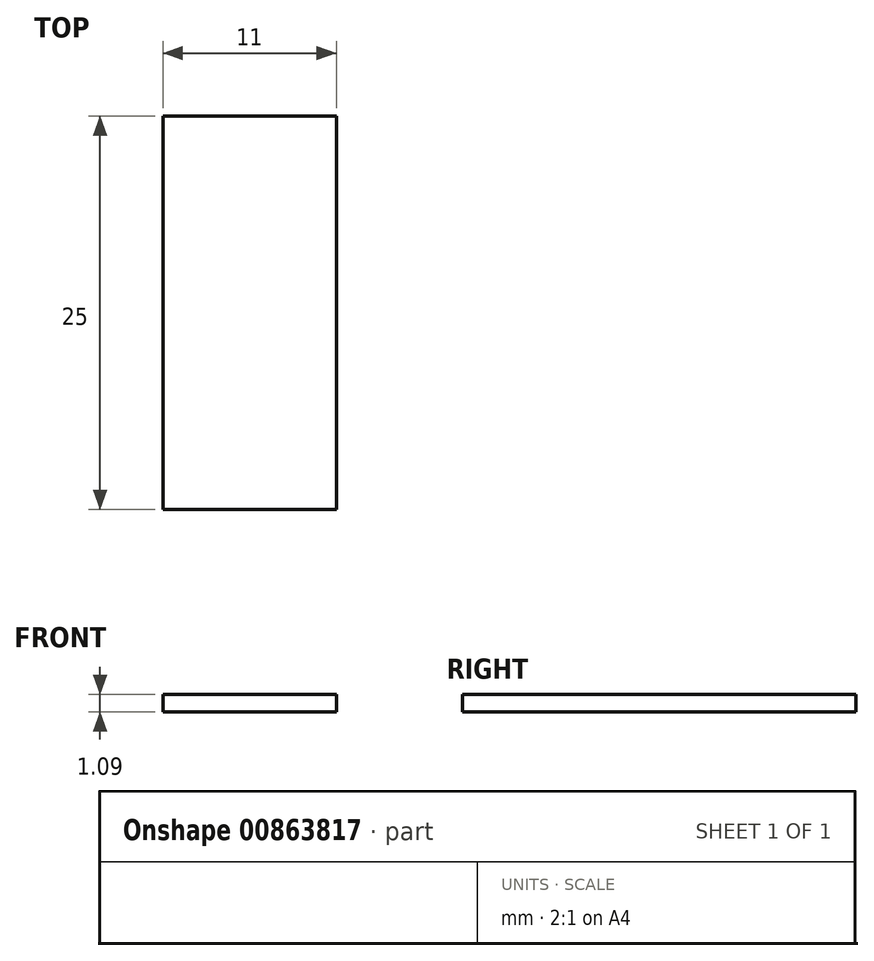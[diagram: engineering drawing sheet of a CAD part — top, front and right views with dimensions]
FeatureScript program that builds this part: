
annotation { "Feature Type Name" : "Feature", "Feature Type Description" : "" }
export const myFeature = defineFeature(function(context is Context, id is Id, definition is map)
    precondition{}
    {
        {
            var Q0;
            Q0=qCreatedBy(makeId("Top.planeOp"),FACE);
            var sketch = newSketch(context, id + "F0", { "sketchPlane" : qUnion([Q0])});
            skLineSegment(sketch, "E0.bottom", {"start": v(0, 0) * mm, "end": v(11, 0) * mm});
            skLineSegment(sketch, "E0.top", {"start": v(0, 25) * mm, "end": v(11, 25) * mm});
            skLineSegment(sketch, "E0.left", {"start": v(0, 0) * mm, "end": v(0, 25) * mm});
            skLineSegment(sketch, "E0.right", {"start": v(11, 0) * mm, "end": v(11, 25) * mm});
            skSolve(sketch);
        }
        {
            var Q0;
            Q0 = qSketchRegion(id + "F0", true);
            extrude(context, id + "F1", {"entities" : qUnion([Q0]), "depth" : 1.09 * mm, "offsetDistance" : 25 * mm});
        }
    });
